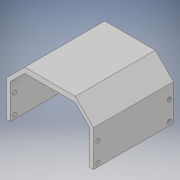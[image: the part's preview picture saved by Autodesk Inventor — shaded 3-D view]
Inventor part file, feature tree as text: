
AUTODESK INVENTOR PART (.ipt)
format: ipt  version: 2017 (Build 210142000, 142)  size: 130,048 bytes
history: native  units: in
note: dims shown in document units (in); Inventor stores cm internally (conversion verified against a paired STEP export)
features: sketch x3, extrude x2, projected_geometry x2, chamfer x1, hole x1
ambient origin geometry x8: Origin, YZ Plane, XZ Plane, XY Plane, X Axis, Y Axis, Z Axis, Center Point
bodies: Solid1 (feature_tree)
feature tree (9):
  extrude  "Extrusion1"  Depth=2.641in
  chamfer  "Chamfer1"  Distance=2.87in
  extrude  "Extrusion2"  Depth=0.125in
  hole  "Hole1"  [1 undecoded]
  sketch  "Sketch1"  dims[d0=1.79in d1=2.641in d2=2.87in d3=0.0in]
  sketch  "Sketch2"  dims[d4=0.6in d5=0.125in d6=45.0deg d12=0.125in]
  projected_geometry  "Projected Loop1"
  sketch  "Sketch3"  dims[d13=0.125in d14=5.0in d15=0.0in d16=2.364in d17=2.641in d18=0.1385in d19=0.63in d20=1.19in d21=0.125in d22=0.125in d23=0.75in d24=0.375in d25=0.25in d26=0.5635in d27=1.0in d28=0.8108in]
  projected_geometry  "Projected Loop2"
note: 1 required parameter value undecoded (feature->parameter linkage not recoverable at this tier; creation-order binding heuristic only, values carry confidence <= 0.55)
